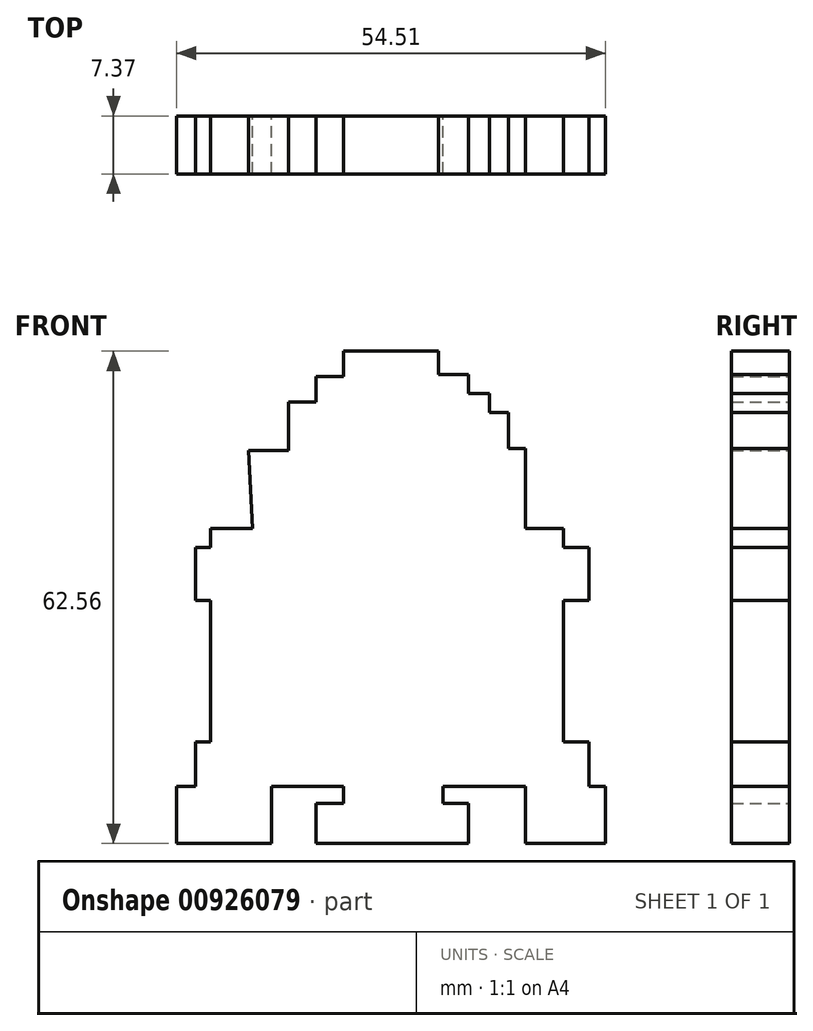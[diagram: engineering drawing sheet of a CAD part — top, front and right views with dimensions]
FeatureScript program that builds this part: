
annotation { "Feature Type Name" : "Feature", "Feature Type Description" : "" }
export const myFeature = defineFeature(function(context is Context, id is Id, definition is map)
    precondition{}
    {
        {
            var Q0;
            Q0=qCreatedBy(makeId("Front.planeOp"),FACE);
            var sketch = newSketch(context, id + "F0", { "sketchPlane" : qUnion([Q0])});
            skLineSegment(sketch, "E0", {"start": v(-3.09, 29.67) * mm, "end": v(4.97, 29.67) * mm});
            skLineSegment(sketch, "E1", {"start": v(4.97, 29.67) * mm, "end": v(4.97, 26.71) * mm});
            skLineSegment(sketch, "E2", {"start": v(4.97, 26.71) * mm, "end": v(8.73, 26.71) * mm});
            skLineSegment(sketch, "E3", {"start": v(-3.09, 29.67) * mm, "end": v(-7.11, 29.67) * mm});
            skLineSegment(sketch, "E4", {"start": v(-7.11, 29.67) * mm, "end": v(-7.11, 26.45) * mm});
            skLineSegment(sketch, "E5", {"start": v(-7.11, 26.45) * mm, "end": v(-10.6, 26.45) * mm});
            skLineSegment(sketch, "E6", {"start": v(-10.6, 26.45) * mm, "end": v(-10.6, 23.22) * mm});
            skLineSegment(sketch, "E7", {"start": v(-10.6, 23.22) * mm, "end": v(-14.1, 23.22) * mm});
            skLineSegment(sketch, "E8", {"start": v(-14.1, 23.22) * mm, "end": v(-14.1, 17.05) * mm});
            skLineSegment(sketch, "E9", {"start": v(-14.1, 17.05) * mm, "end": v(-19.2, 17.05) * mm});
            skLineSegment(sketch, "E10", {"start": v(8.73, 26.71) * mm, "end": v(8.73, 24.3) * mm});
            skLineSegment(sketch, "E11", {"start": v(8.73, 24.3) * mm, "end": v(11.41, 24.3) * mm});
            skLineSegment(sketch, "E12", {"start": v(11.41, 24.3) * mm, "end": v(11.41, 21.88) * mm});
            skLineSegment(sketch, "E13", {"start": v(11.41, 21.88) * mm, "end": v(13.83, 21.88) * mm});
            skLineSegment(sketch, "E14", {"start": v(13.83, 21.88) * mm, "end": v(13.83, 17.32) * mm});
            skLineSegment(sketch, "E15", {"start": v(13.83, 17.32) * mm, "end": v(15.98, 17.32) * mm});
            skLineSegment(sketch, "E16", {"start": v(15.98, 17.32) * mm, "end": v(15.98, 7.11) * mm});
            skLineSegment(sketch, "E17", {"start": v(15.98, 7.11) * mm, "end": v(20.8, 7.11) * mm});
            skLineSegment(sketch, "E18", {"start": v(20.8, 7.11) * mm, "end": v(20.8, 4.7) * mm});
            skLineSegment(sketch, "E19", {"start": v(20.8, 4.7) * mm, "end": v(24.03, 4.7) * mm});
            skLineSegment(sketch, "E20", {"start": v(24.03, 4.7) * mm, "end": v(24.03, -2.01) * mm});
            skLineSegment(sketch, "E21", {"start": v(24.03, -2.01) * mm, "end": v(20.8, -2.01) * mm});
            skLineSegment(sketch, "E22", {"start": v(20.8, -2.01) * mm, "end": v(20.8, -20) * mm});
            skLineSegment(sketch, "E23", {"start": v(20.8, -20) * mm, "end": v(24.03, -20) * mm});
            skLineSegment(sketch, "E24", {"start": v(24.03, -20) * mm, "end": v(24.03, -25.64) * mm});
            skLineSegment(sketch, "E25", {"start": v(24.03, -25.64) * mm, "end": v(26.18, -25.64) * mm});
            skLineSegment(sketch, "E26", {"start": v(26.18, -25.64) * mm, "end": v(26.18, -32.9) * mm});
            skLineSegment(sketch, "E27", {"start": v(26.18, -32.9) * mm, "end": v(15.98, -32.9) * mm});
            skLineSegment(sketch, "E28", {"start": v(15.98, -32.9) * mm, "end": v(15.98, -25.64) * mm});
            skLineSegment(sketch, "E29", {"start": v(15.98, -25.64) * mm, "end": v(5.5, -25.64) * mm});
            skLineSegment(sketch, "E30", {"start": v(5.5, -25.64) * mm, "end": v(5.5, -27.79) * mm});
            skLineSegment(sketch, "E31", {"start": v(5.5, -27.79) * mm, "end": v(8.73, -27.79) * mm});
            skLineSegment(sketch, "E32", {"start": v(8.73, -27.79) * mm, "end": v(8.73, -32.9) * mm});
            skLineSegment(sketch, "E33", {"start": v(8.73, -32.9) * mm, "end": v(-10.6, -32.9) * mm});
            skLineSegment(sketch, "E34", {"start": v(-10.6, -32.9) * mm, "end": v(-10.6, -27.79) * mm});
            skLineSegment(sketch, "E35", {"start": v(-10.6, -27.79) * mm, "end": v(-7.11, -27.79) * mm});
            skLineSegment(sketch, "E36", {"start": v(-7.11, -27.79) * mm, "end": v(-7.11, -25.64) * mm});
            skLineSegment(sketch, "E37", {"start": v(-7.11, -25.64) * mm, "end": v(-16.24, -25.64) * mm});
            skLineSegment(sketch, "E38", {"start": v(-16.24, -25.64) * mm, "end": v(-16.24, -32.9) * mm});
            skLineSegment(sketch, "E39", {"start": v(-16.24, -32.9) * mm, "end": v(-28.33, -32.9) * mm});
            skLineSegment(sketch, "E40", {"start": v(-28.33, -32.9) * mm, "end": v(-28.33, -27.79) * mm});
            skLineSegment(sketch, "E41", {"start": v(-28.33, -27.79) * mm, "end": v(-28.33, -25.64) * mm});
            skLineSegment(sketch, "E42", {"start": v(-28.33, -25.64) * mm, "end": v(-25.9, -25.64) * mm});
            skLineSegment(sketch, "E43", {"start": v(-25.9, -25.64) * mm, "end": v(-25.9, -20) * mm});
            skLineSegment(sketch, "E44", {"start": v(-25.9, -20) * mm, "end": v(-24.03, -20) * mm});
            skLineSegment(sketch, "E45", {"start": v(-24.03, -20) * mm, "end": v(-24.03, -2.01) * mm});
            skLineSegment(sketch, "E46", {"start": v(-24.03, -2.01) * mm, "end": v(-25.9, -2.01) * mm});
            skLineSegment(sketch, "E47", {"start": v(-25.9, -2.01) * mm, "end": v(-25.9, 4.7) * mm});
            skLineSegment(sketch, "E48", {"start": v(-25.9, 4.7) * mm, "end": v(-24.03, 4.7) * mm});
            skLineSegment(sketch, "E49", {"start": v(-24.03, 4.7) * mm, "end": v(-24.03, 7.11) * mm});
            skLineSegment(sketch, "E50", {"start": v(-24.03, 7.11) * mm, "end": v(-18.66, 7.11) * mm});
            skLineSegment(sketch, "E51", {"start": v(-18.66, 7.11) * mm, "end": v(-19.2, 17.05) * mm});
            skSolve(sketch);
        }
        {
            var Q0;
            Q0 = qSketchRegion(id + "F0", true);
            extrude(context, id + "F1", {"entities" : qUnion([Q0]), "depth" : 7.37 * mm, "offsetDistance" : 25.4 * mm});
        }
    });
